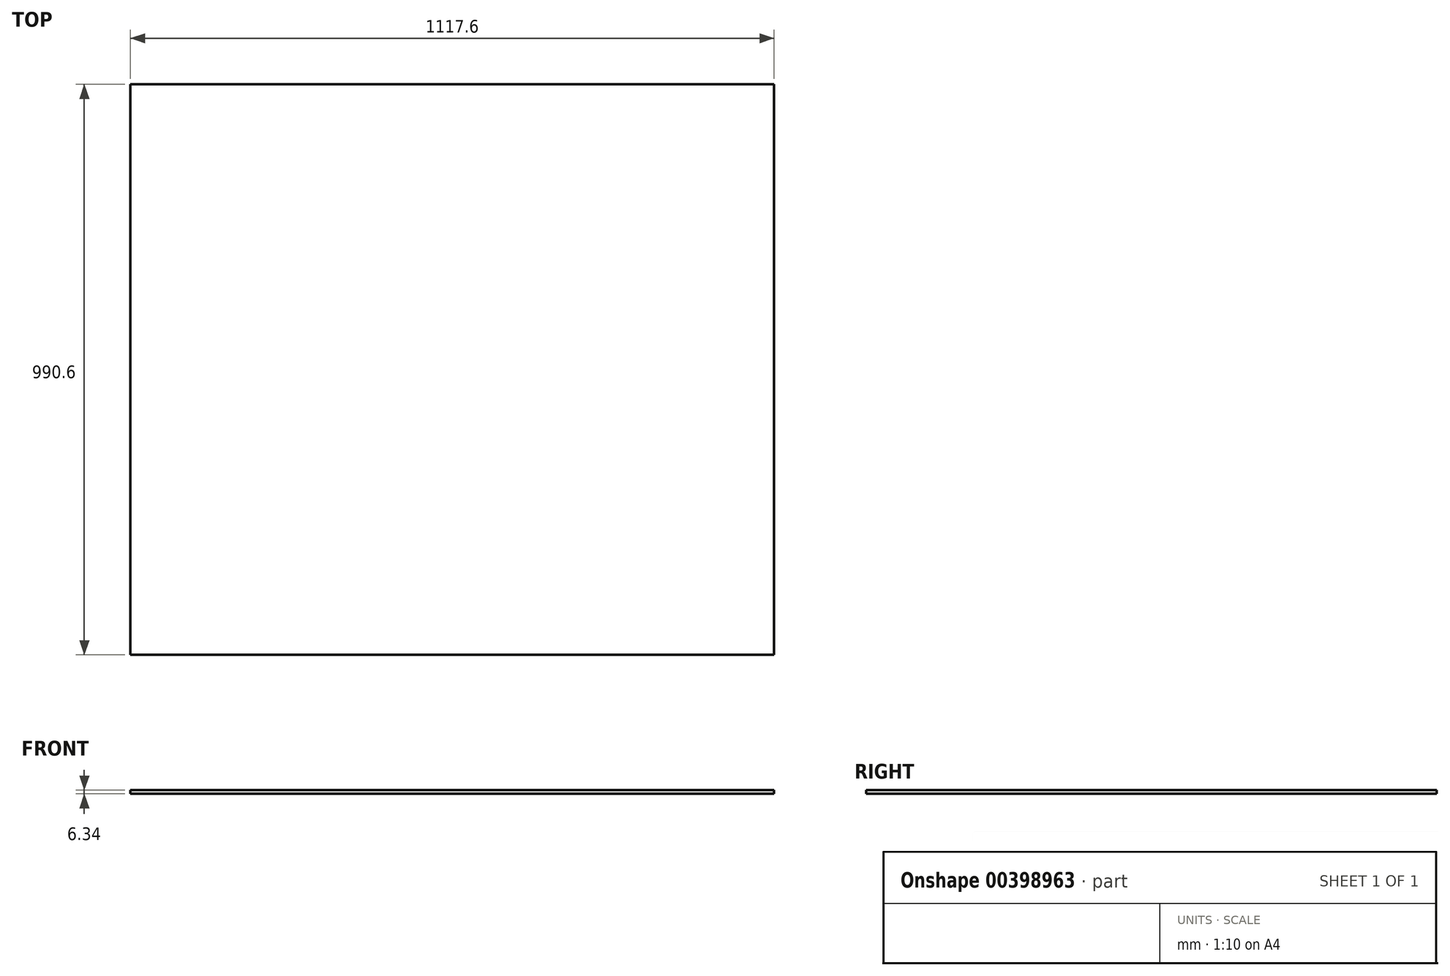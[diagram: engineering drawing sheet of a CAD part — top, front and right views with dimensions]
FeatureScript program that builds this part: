
annotation { "Feature Type Name" : "Feature", "Feature Type Description" : "" }
export const myFeature = defineFeature(function(context is Context, id is Id, definition is map)
    precondition{}
    {
        {
            var Q0;
            Q0=qCreatedBy(makeId("Top.planeOp"),FACE);
            var sketch = newSketch(context, id + "F0", { "sketchPlane" : qUnion([Q0])});
            skLineSegment(sketch, "E0.bottom", {"start": v(558.8, 495.3) * mm, "end": v(-558.8, 495.3) * mm});
            skLineSegment(sketch, "E0.top", {"start": v(558.8, -495.3) * mm, "end": v(-558.8, -495.3) * mm});
            skLineSegment(sketch, "E0.left", {"start": v(558.8, 495.3) * mm, "end": v(558.8, -495.3) * mm});
            skLineSegment(sketch, "E0.right", {"start": v(-558.8, 495.3) * mm, "end": v(-558.8, -495.3) * mm});
            skPoint(sketch, "E0.middle", {"position": v(0, 0) * mm});
            skSolve(sketch);
        }
        {
            var Q0;
            Q0 = qSketchRegion(id + "F0", true);
            extrude(context, id + "F1", {"entities" : qUnion([Q0]), "depth" : 6.35 * mm, "symmetric" : true});
        }
    });
